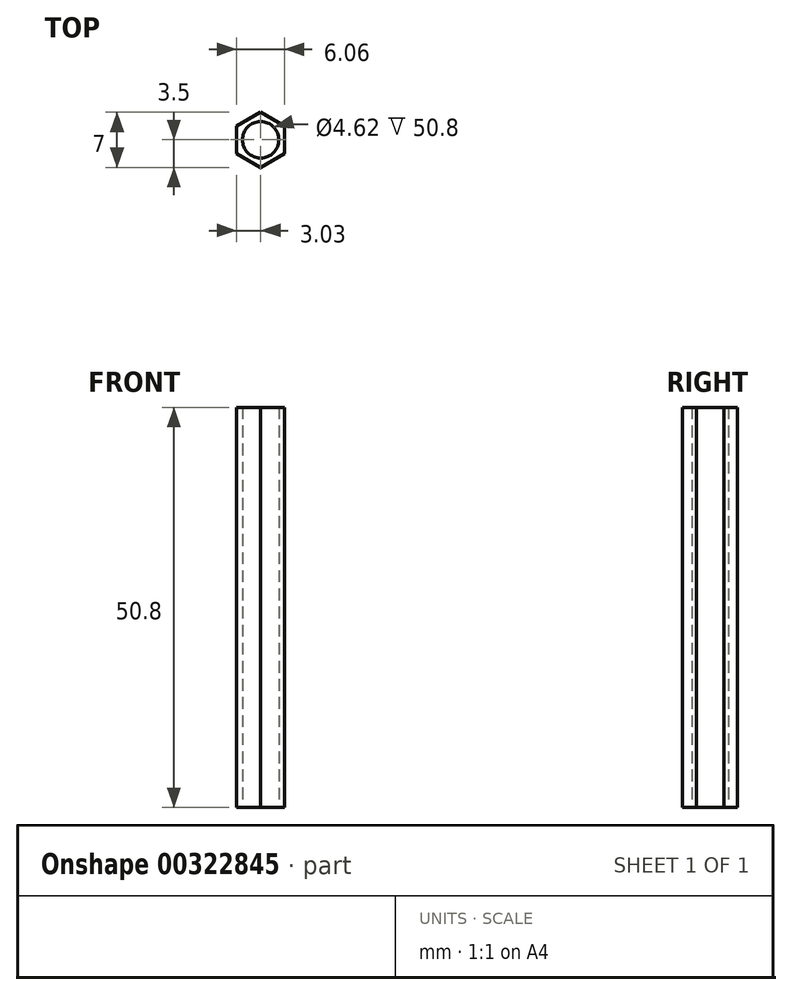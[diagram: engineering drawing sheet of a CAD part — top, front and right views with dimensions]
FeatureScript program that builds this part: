
annotation { "Feature Type Name" : "Feature", "Feature Type Description" : "" }
export const myFeature = defineFeature(function(context is Context, id is Id, definition is map)
    precondition{}
    {
        {
            var Q0;
            Q0=qCreatedBy(makeId("Top.planeOp"),FACE);
            var sketch = newSketch(context, id + "F0", { "sketchPlane" : qUnion([Q0])});
            skLineSegment(sketch, "E0.0", {"start": v(0, 3.5) * mm, "end": v(3.03, 1.75) * mm});
            skLineSegment(sketch, "E0.1", {"start": v(3.03, 1.75) * mm, "end": v(3.03, -1.75) * mm});
            skLineSegment(sketch, "E0.2", {"start": v(3.03, -1.75) * mm, "end": v(0, -3.5) * mm});
            skLineSegment(sketch, "E0.3", {"start": v(0, -3.5) * mm, "end": v(-3.03, -1.75) * mm});
            skLineSegment(sketch, "E0.4", {"start": v(-3.03, -1.75) * mm, "end": v(-3.03, 1.75) * mm});
            skLineSegment(sketch, "E0.5", {"start": v(-3.03, 1.75) * mm, "end": v(0, 3.5) * mm});
            skPoint(sketch, "E0.cCircle.center.orphan", {"position": v(0, 0) * mm});
            skCircle(sketch, "E1", {"center": v(0, 0) * mm, "radius": 2.31 * mm});
            skSolve(sketch);
        }
        {
            var Q0;
            Q0=qSketchRegion(id+"F0",true);
            extrude(context, id + "F1", {"entities" : qUnion([Q0]), "depth" : 50.8 * mm});
        }
        {
            var Q0;
            Q0=makeQuery(id+"F1.opExtrude","SWEPT_BODY",BODY,{"disambiguationData":[OSD([sQuery(id+"F0.wireOp",EDGE,"E0.0"),sQuery(id+"F0.wireOp",EDGE,"E0.1"),sQuery(id+"F0.wireOp",EDGE,"E0.2"),sQuery(id+"F0.wireOp",EDGE,"E0.3"),sQuery(id+"F0.wireOp",EDGE,"E0.4"),sQuery(id+"F0.wireOp",EDGE,"E0.5"),sQuery(id+"F0.wireOp",EDGE,"E1")])]});
            transform(context, id + "F2", {"entities" : qUnion([Q0]), "transformType" : TransformType.TRANSLATION_3D, "dx" : 0 * mm, "dy" : 0 * mm, "dz" : -25.4 * mm, "makeCopy" : false});
        }
    });
